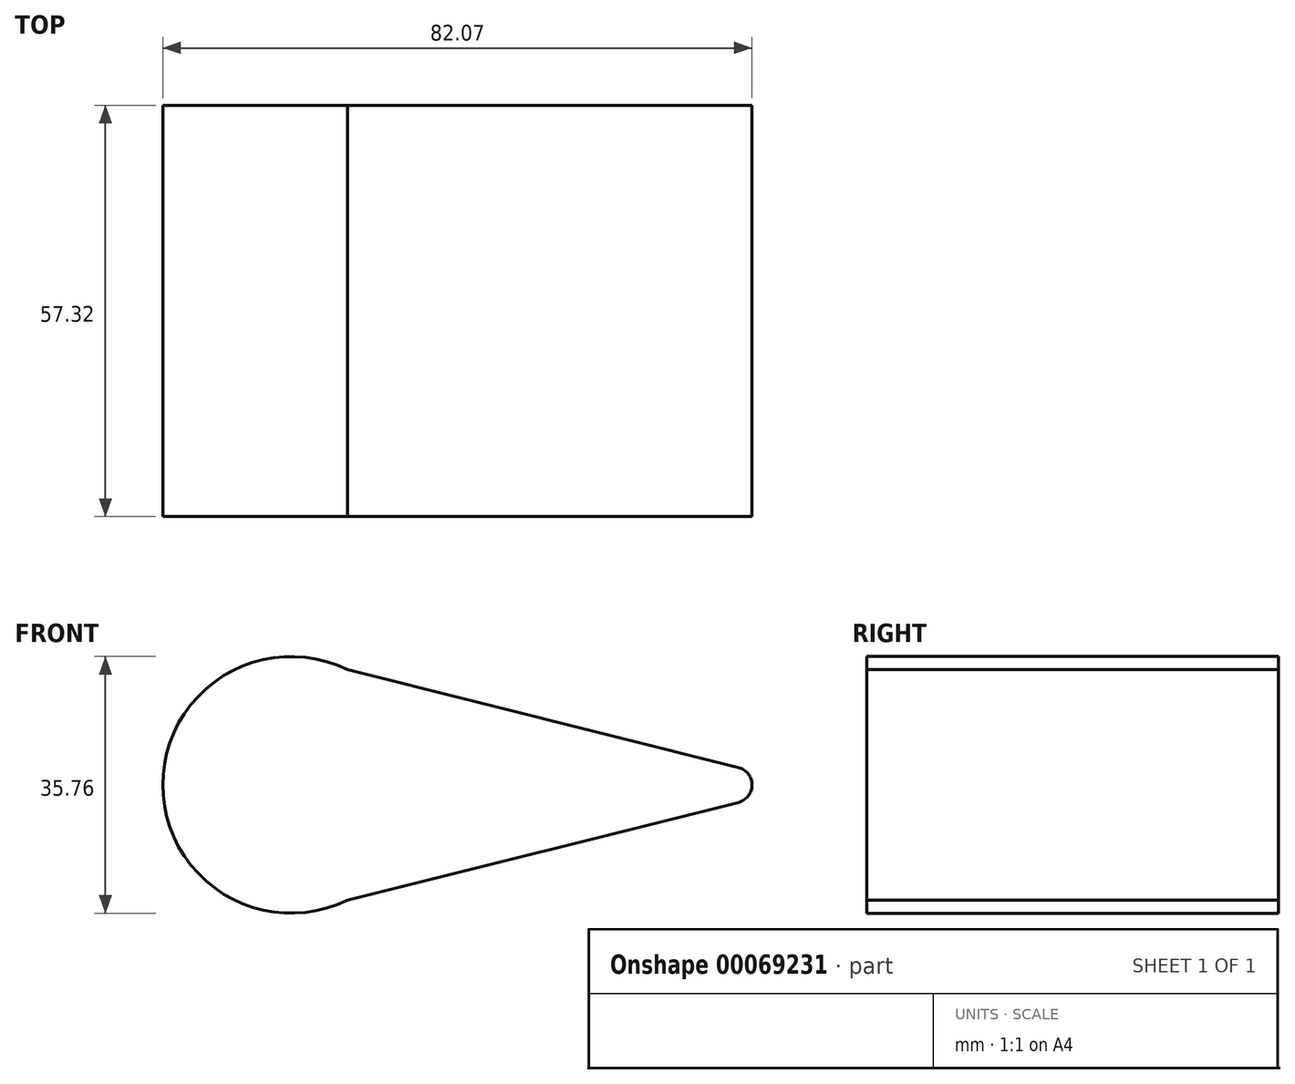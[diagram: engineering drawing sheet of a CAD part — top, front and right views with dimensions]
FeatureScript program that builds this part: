
annotation { "Feature Type Name" : "Feature", "Feature Type Description" : "" }
export const myFeature = defineFeature(function(context is Context, id is Id, definition is map)
    precondition{}
    {
        {
            var Q0;
            Q0=qCreatedBy(makeId("Front.planeOp"),FACE);
            var sketch = newSketch(context, id + "F0", { "sketchPlane" : qUnion([Q0])});
            skCircle(sketch, "E0", {"center": v(0, 0) * mm, "radius": 17.88 * mm});
            skCircle(sketch, "E1", {"center": v(61.68, 0) * mm, "radius": 2.52 * mm});
            skLineSegment(sketch, "E2", {"start": v(7.85, 16.06) * mm, "end": v(62.29, 2.44) * mm});
            skLineSegment(sketch, "E3", {"start": v(7.85, -16.06) * mm, "end": v(62.29, -2.44) * mm});
            skSolve(sketch);
        }
        {
            var Q0;
            {var subQ0=sQuery(id+"F0.wireOp",EDGE,"E2");Q0=makeQuery(id+"F0.imprint","IMPRINT",FACE,{"disambiguationData":[TD([[makeQuery(id+"F0.imprint","IMPRINT",EDGE,{"derivedFrom":subQ0}),-1.0]])]});}
            var Q1;
            {var subQ0=sQuery(id+"F0.wireOp",EDGE,"E1");var subQ1=makeQuery(id+"F0.imprint","INTERSECT",VERTEX,{"derivedFrom":[subQ0,sQuery(id+"F0.wireOp",EDGE,"E2")]});Q1=makeQuery(id+"F0.imprint","IMPRINT",FACE,{"disambiguationData":[TD([[makeQuery(id+"F0.imprint","IMPRINT",EDGE,{"disambiguationData":[TD([[subQ1,-1.0]])],"derivedFrom":subQ0}),1.0]])]});}
            var Q2;
            {var subQ0=sQuery(id+"F0.wireOp",EDGE,"E0");var subQ1=makeQuery(id+"F0.imprint","INTERSECT",VERTEX,{"derivedFrom":[subQ0,sQuery(id+"F0.wireOp",EDGE,"E2")]});Q2=makeQuery(id+"F0.imprint","IMPRINT",FACE,{"disambiguationData":[TD([[makeQuery(id+"F0.imprint","IMPRINT",EDGE,{"disambiguationData":[TD([[subQ1,-1.0]])],"derivedFrom":subQ0}),1.0]])]});}
            extrude(context, id + "F1", {"entities" : qUnion([Q0, Q1, Q2]), "depth" : 57.32 * mm});
        }
    });
